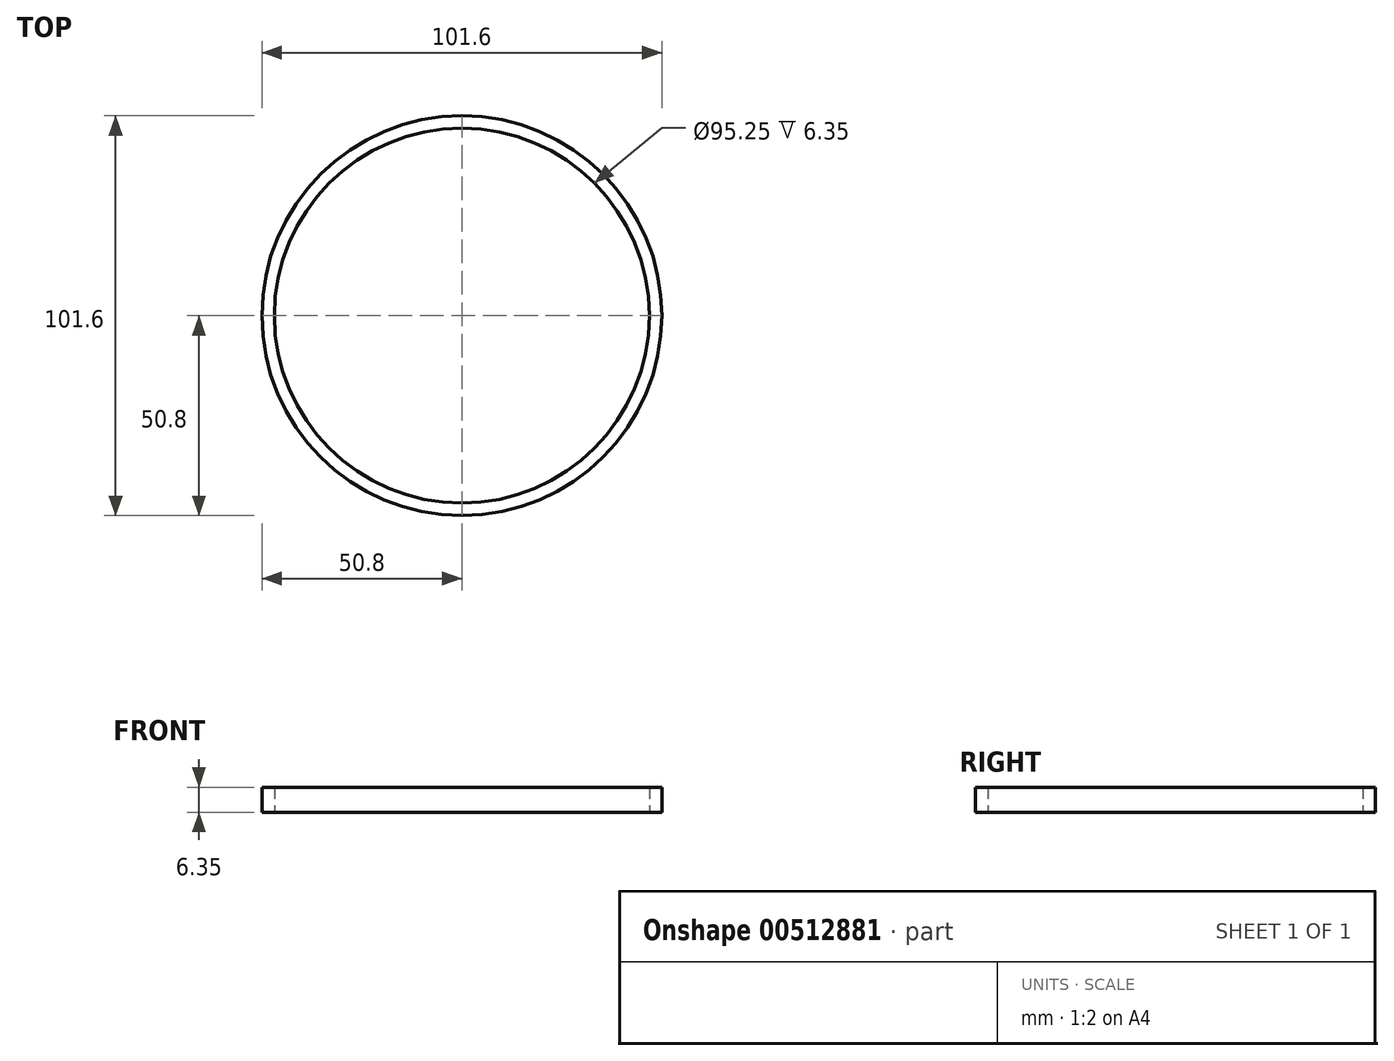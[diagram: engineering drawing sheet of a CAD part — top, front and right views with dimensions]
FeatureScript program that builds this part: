
annotation { "Feature Type Name" : "Feature", "Feature Type Description" : "" }
export const myFeature = defineFeature(function(context is Context, id is Id, definition is map)
    precondition{}
    {
        {
            var Q0;
            Q0=qCreatedBy(makeId("Top.planeOp"),FACE);
            var sketch = newSketch(context, id + "F0", { "sketchPlane" : qUnion([Q0])});
            skCircle(sketch, "E0", {"center": v(0, 0) * mm, "radius": 50.8 * mm});
            skCircle(sketch, "E1.0", {"center": v(0, 0) * mm, "radius": 47.63 * mm});
            skSolve(sketch);
        }
        {
            var Q0;
            Q0=makeQuery(id+"F0.imprint","IMPRINT",FACE,{"disambiguationData":[TD([[makeQuery(id+"F0.imprint","IMPRINT",EDGE,{"derivedFrom":sQuery(id+"F0.wireOp",EDGE,"E0")}),1.0]])]});
            extrude(context, id + "F1", {"entities" : qUnion([Q0]), "depth" : 6.35 * mm});
        }
    });
